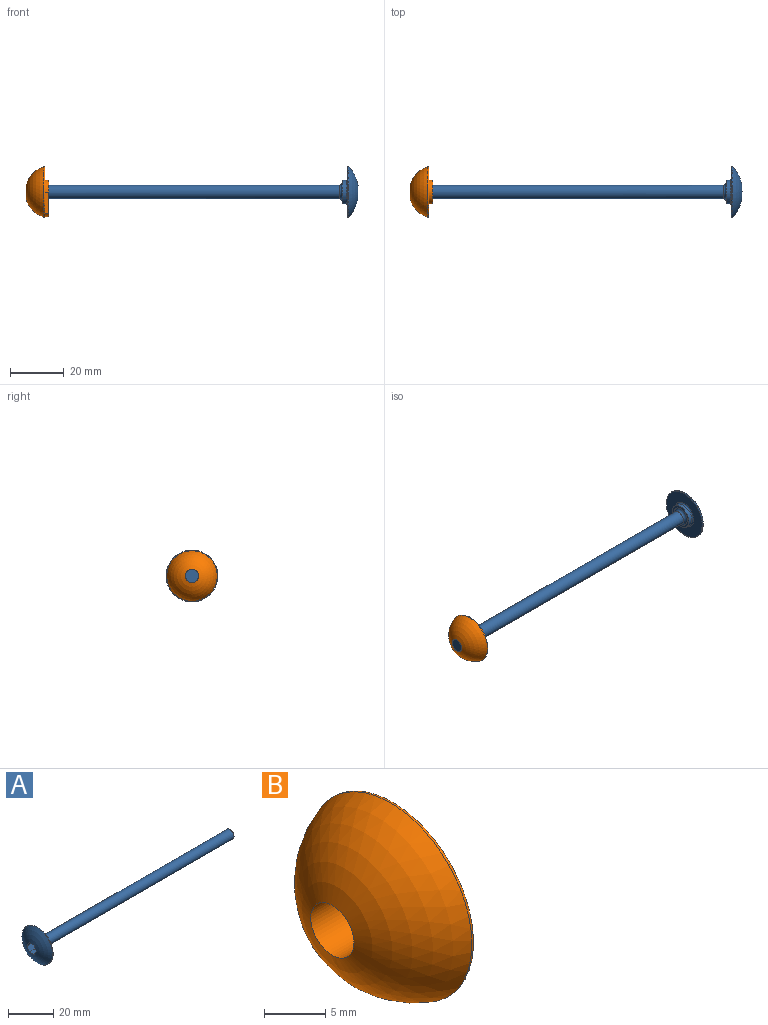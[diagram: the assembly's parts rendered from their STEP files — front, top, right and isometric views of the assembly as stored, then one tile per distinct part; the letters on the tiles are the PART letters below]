
ASSEMBLY  parts=2 mates=1
PART A: 16 faces, bbox 123.9x20.8x20.8 mm
  f0: plane 8.9x8.9mm, normal (1,0,0), area 23.7mm2, adj f1,f8
  f1: cylinder r=4.45mm len=8.9mm, axis (-1,0,0), area 41.9mm2, adj f0,f7
  f2: plane 18.75x18.75mm, normal (1,0,0), area 199.3mm2, adj f6,f7
  f3: sphere r=14.14mm, area 307.6mm2, adj f6,f9,f10,f11,f12,f13,f14
  f4: plane 5x5mm, normal (1,0,0), area 19.6mm2, adj f5
  f5: cylinder r=2.5mm len=117mm, axis (-1,0,0), area 1837.8mm2, adj f4,f8
  f6: torus R=9.38mm, axis (-1,0,0), area 36mm2, adj f2,f3
  f7: torus R=4.95mm, axis (-1,0,0), area 22.9mm2, adj f1,f2
  f8: torus R=3.5mm, axis (1,0,0), area 28.3mm2, adj f0,f5
  f9: plane 3.78x2.5mm, normal (0,0.87,0.5), area 10.8mm2, adj f3,f10,f14,f15
  f10: plane 3.78x2.89mm, normal (0,0,1), area 10.8mm2, adj f3,f9,f11,f15
  f11: plane 3.78x2.5mm, normal (0,-0.87,0.5), area 10.8mm2, adj f3,f10,f12,f15
  f12: plane 3.78x2.5mm, normal (0,-0.87,-0.5), area 10.8mm2, adj f3,f11,f13,f15
  f13: plane 3.78x2.89mm, normal (0,0,-1), area 10.8mm2, adj f3,f12,f14,f15
  f14: plane 3.78x2.5mm, normal (0,0.87,-0.5), area 10.8mm2, adj f3,f9,f13,f15
  f15: plane 5.77x5mm, normal (-1,0,0), area 21.7mm2, adj f9,f10,f11,f12,f13,f14
PART B: 9 faces, bbox 8.5x20.4x20.4 mm
  f0: cylinder r=4.45mm len=8.9mm, axis (1,0,0), area 21mm2, adj f2,f4,f7,f8
  f1: cylinder r=9.17mm len=8.9mm, axis (-1,0,0), area 13.9mm2, adj f2,f6,f7,f8
  f2: plane 8.02x1.5mm, normal (0,1,0), area 12mm2, adj f0,f1,f4,f8
  f3: cylinder r=2.5mm len=8.52mm, axis (1,0,0), area 133.8mm2, adj f5,f8
  f4: plane 18.34x17.19mm, normal (1,0,0), area 154.8mm2, adj f0,f2,f6,f7
  f5: sphere r=9.82mm, area 413.1mm2, adj f3,f6
  f6: torus R=9.17mm, axis (1,0,0), area 27.3mm2, adj f1,f4,f5
  f7: plane 8.02x1.5mm, normal (0,-1,0), area 12mm2, adj f0,f1,f4,f8
  f8: plane 13.62x8.9mm, normal (1,0,0), area 89.8mm2, adj f0,f1,f2,f3,f7
PLACE A rot(axis=(0,1,0),180deg) t=(107.24,58.24,-22.58)mm
PLACE B t=(-9.88,58.24,-22.58)mm
MATE fastened B.f3 <-> A.f1  axis (1,0,0) through (-16.9,58.24,-22.58)mm
